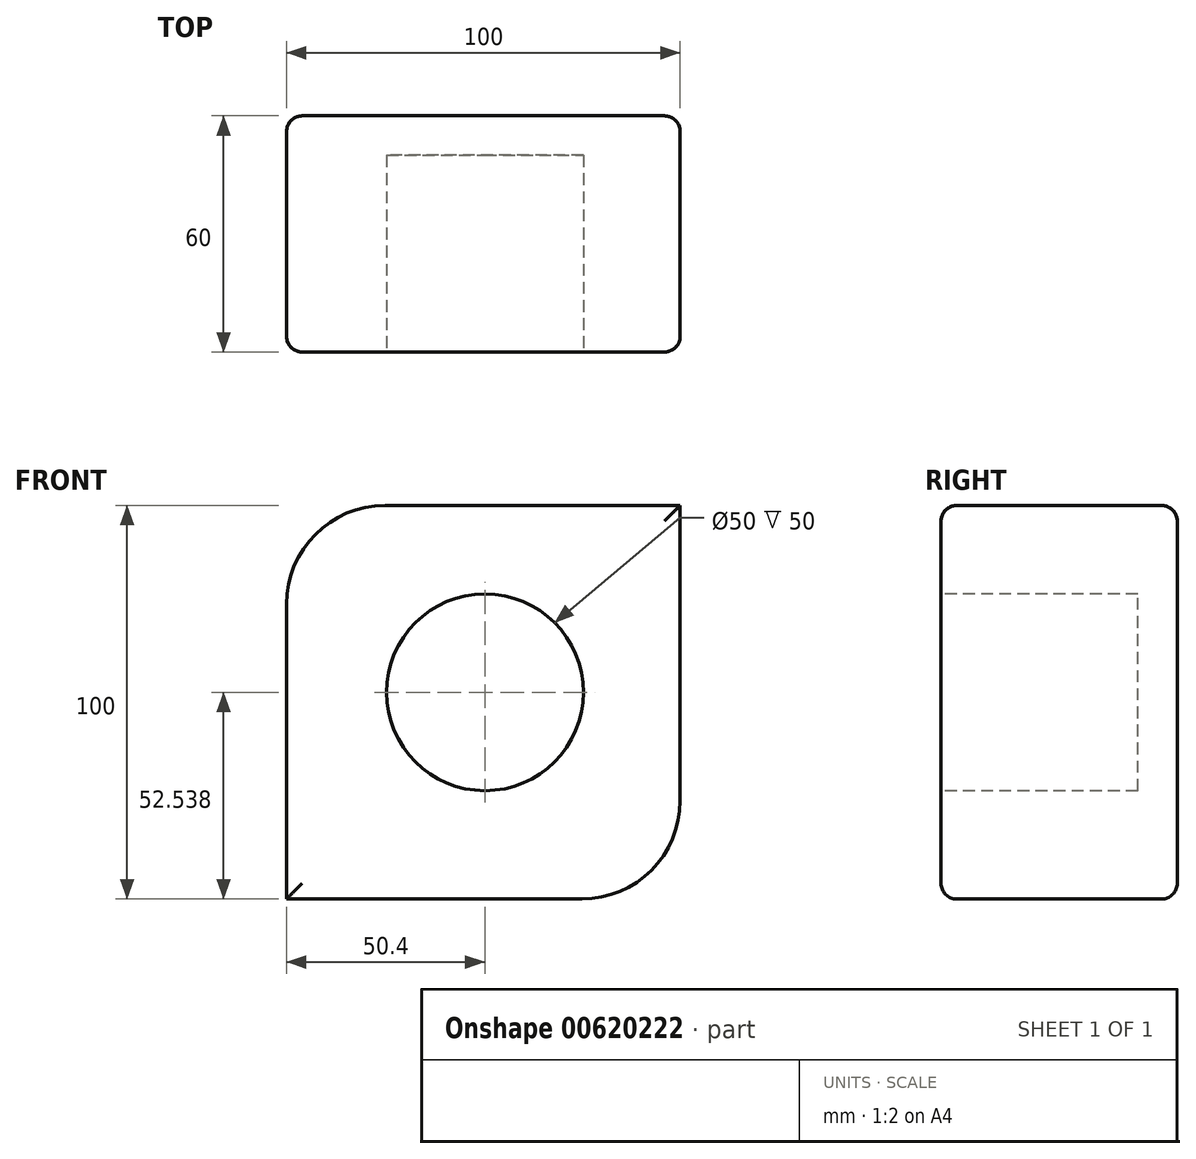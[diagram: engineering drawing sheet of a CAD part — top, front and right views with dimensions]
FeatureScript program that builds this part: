
annotation { "Feature Type Name" : "Feature", "Feature Type Description" : "" }
export const myFeature = defineFeature(function(context is Context, id is Id, definition is map)
    precondition{}
    {
        {
            var Q0;
            Q0=qCreatedBy(makeId("Front.planeOp"),FACE);
            var sketch = newSketch(context, id + "F0", { "sketchPlane" : qUnion([Q0])});
            skLineSegment(sketch, "E0.bottom", {"start": v(-25.4, 69.83) * mm, "end": v(49.6, 69.83) * mm});
            skLineSegment(sketch, "E0.top", {"start": v(-50.4, -30.17) * mm, "end": v(24.6, -30.17) * mm});
            skLineSegment(sketch, "E0.left", {"start": v(-50.4, 44.83) * mm, "end": v(-50.4, -30.17) * mm});
            skLineSegment(sketch, "E0.right", {"start": v(49.6, 69.83) * mm, "end": v(49.6, -5.17) * mm});
            skPoint(sketch, "E1.visualSharp", {"position": v(-50.4, 69.83) * mm});
            skArc(sketch, "E1.filletArc", {"start": v(-25.4, 69.83) * mm, "mid": v(-43.08, 62.51) * mm, "end": v(-50.4, 44.83) * mm});
            skPoint(sketch, "E2.visualSharp", {"position": v(49.6, -30.17) * mm});
            skArc(sketch, "E2.filletArc", {"start": v(24.6, -30.17) * mm, "mid": v(42.27, -22.85) * mm, "end": v(49.6, -5.17) * mm});
            skSolve(sketch);
        }
        {
            var Q0;
            Q0=makeQuery(id+"F0.imprint","IMPRINT",FACE,{"disambiguationData":[TD([[makeQuery(id+"F0.imprint","IMPRINT",EDGE,{"derivedFrom":sQuery(id+"F0.wireOp",EDGE,"E0.bottom")}),-1.0]])]});
            extrude(context, id + "F1", {"entities" : qUnion([Q0]), "depth" : 60 * mm, "offsetDistance" : 25 * mm});
        }
        {
            var Q0;
            Q0=makeQuery(id+"F1.opExtrude","CAP_FACE",FACE,{"disambiguationData":[OSD([sQuery(id+"F0.wireOp",EDGE,"E0.bottom"),sQuery(id+"F0.wireOp",EDGE,"E0.top"),sQuery(id+"F0.wireOp",EDGE,"E0.left"),sQuery(id+"F0.wireOp",EDGE,"E0.right"),sQuery(id+"F0.wireOp",EDGE,"E1.filletArc"),sQuery(id+"F0.wireOp",EDGE,"E2.filletArc")])],"isStart":false});
            fillet(context, id + "F2", {"entities" : qUnion([Q0]), "radius" : 4 * mm, "tangentPropagation" : true, "allowEdgeOverflow" : false});
        }
        {
            var Q0;
            Q0=makeQuery(id+"F1.opExtrude","CAP_FACE",FACE,{"disambiguationData":[OSD([sQuery(id+"F0.wireOp",EDGE,"E0.bottom"),sQuery(id+"F0.wireOp",EDGE,"E0.top"),sQuery(id+"F0.wireOp",EDGE,"E0.left"),sQuery(id+"F0.wireOp",EDGE,"E0.right"),sQuery(id+"F0.wireOp",EDGE,"E1.filletArc"),sQuery(id+"F0.wireOp",EDGE,"E2.filletArc")])],"isStart":true});
            fillet(context, id + "F3", {"entities" : qUnion([Q0]), "radius" : 4 * mm, "tangentPropagation" : true, "allowEdgeOverflow" : false});
        }
        {
            var Q0;
            Q0=makeQuery(id+"F1.opExtrude","CAP_FACE",FACE,{"disambiguationData":[OSD([sQuery(id+"F0.wireOp",EDGE,"E0.bottom"),sQuery(id+"F0.wireOp",EDGE,"E0.top"),sQuery(id+"F0.wireOp",EDGE,"E0.left"),sQuery(id+"F0.wireOp",EDGE,"E0.right"),sQuery(id+"F0.wireOp",EDGE,"E1.filletArc"),sQuery(id+"F0.wireOp",EDGE,"E2.filletArc")])],"isStart":false});
            var sketch = newSketch(context, id + "F4", { "sketchPlane" : qUnion([Q0])});
            skCircle(sketch, "E3", {"center": v(0, 22.37) * mm, "radius": 25 * mm});
            skSolve(sketch);
        }
        {
            var Q0;
            Q0 = qSketchRegion(id + "F4", true);
            extrude(context, id + "F5", {"entities" : qUnion([Q0]), "operationType" : NewBodyOperationType.REMOVE, "oppositeDirection" : true, "depth" : 25 * mm, "offsetDistance" : 25 * mm});
        }
        {
            var Q0;
            Q0=makeQuery(id+"F5.boolean.opBoolean","COPY",FACE,{"derivedFrom":makeQuery(id+"F5.opExtrude","CAP_FACE",FACE,{"disambiguationData":[OSD([sQuery(id+"F4.wireOp",EDGE,"E3")])],"isStart":false})});
            var Q1;
            Q1=makeQuery(id+"F4.imprint","IMPRINT",FACE,{"disambiguationData":[TD([[makeQuery(id+"F4.imprint","IMPRINT",EDGE,{"derivedFrom":sQuery(id+"F4.wireOp",EDGE,"E3")}),1.0]])]});
            extrude(context, id + "F6", {"entities" : qUnion([Q0, Q1]), "operationType" : NewBodyOperationType.REMOVE, "oppositeDirection" : true, "depth" : 25 * mm, "offsetDistance" : 25 * mm});
        }
    });
